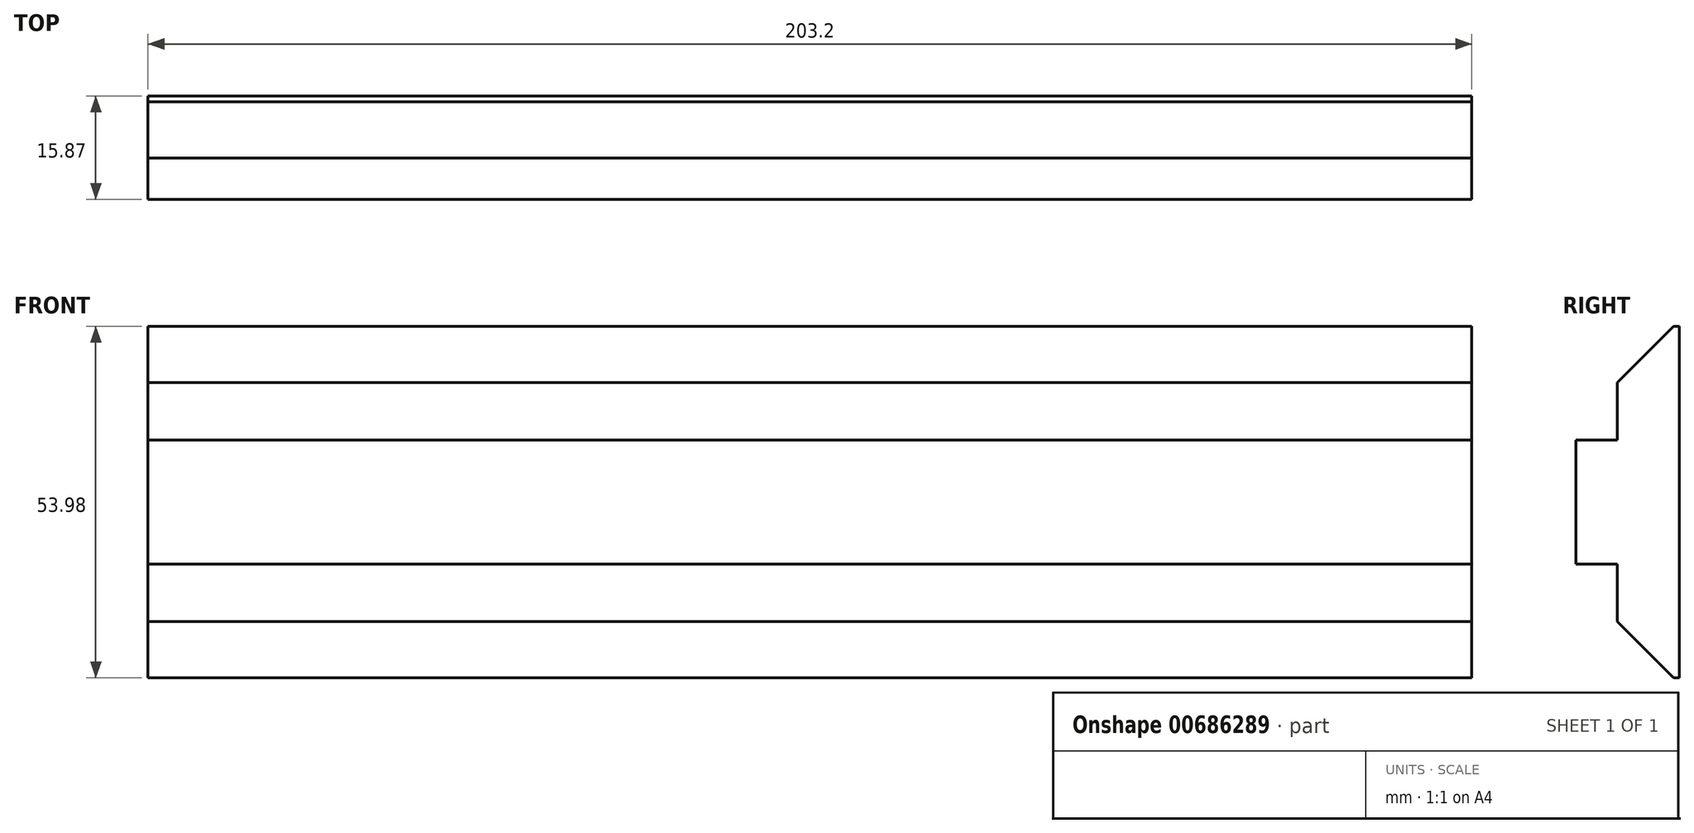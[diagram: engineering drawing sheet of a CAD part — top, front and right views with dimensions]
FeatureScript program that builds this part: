
annotation { "Feature Type Name" : "Feature", "Feature Type Description" : "" }
export const myFeature = defineFeature(function(context is Context, id is Id, definition is map)
    precondition{}
    {
        {
            var Q0;
            Q0=qCreatedBy(makeId("Front.planeOp"),FACE);
            var sketch = newSketch(context, id + "F0", { "sketchPlane" : qUnion([Q0])});
            skLineSegment(sketch, "E0.bottom", {"start": v(101.6, 26.99) * mm, "end": v(-101.6, 26.99) * mm});
            skLineSegment(sketch, "E0.top", {"start": v(101.6, -26.99) * mm, "end": v(-101.6, -26.99) * mm});
            skLineSegment(sketch, "E0.left", {"start": v(101.6, 26.99) * mm, "end": v(101.6, -26.99) * mm});
            skLineSegment(sketch, "E0.right", {"start": v(-101.6, 26.99) * mm, "end": v(-101.6, -26.99) * mm});
            skPoint(sketch, "E0.middle", {"position": v(0, 0) * mm});
            skSolve(sketch);
        }
        {
            var Q0;
            Q0=makeQuery(id+"F0.imprint","IMPRINT",FACE,{"disambiguationData":[TD([[makeQuery(id+"F0.imprint","IMPRINT",EDGE,{"derivedFrom":sQuery(id+"F0.wireOp",EDGE,"E0.bottom")}),1.0]])]});
            extrude(context, id + "F1", {"entities" : qUnion([Q0]), "endBound" : BoundingType.SYMMETRIC, "depth" : 9.52 * mm, "offsetDistance" : 25.4 * mm});
        }
        {
            var Q0;
            Q0=makeQuery(id+"F1.opExtrude","CAP_EDGE",EDGE,{"disambiguationData":[OSD([sQuery(id+"F0.wireOp",EDGE,"E0.bottom")])],"isStart":false});
            var Q1;
            Q1=makeQuery(id+"F1.opExtrude","CAP_EDGE",EDGE,{"disambiguationData":[OSD([sQuery(id+"F0.wireOp",EDGE,"E0.top")])],"isStart":false});
            chamfer(context, id + "F2", {"entities" : qUnion([Q0, Q1]), "width" : 8.64 * mm, "tangentPropagation" : true});
        }
        {
            var Q0;
            Q0=makeQuery(id+"F1.opExtrude","CAP_FACE",FACE,{"disambiguationData":[OSD([sQuery(id+"F0.wireOp",EDGE,"E0.bottom"),sQuery(id+"F0.wireOp",EDGE,"E0.top"),sQuery(id+"F0.wireOp",EDGE,"E0.left"),sQuery(id+"F0.wireOp",EDGE,"E0.right")])],"isStart":false});
            var sketch = newSketch(context, id + "F3", { "sketchPlane" : qUnion([Q0])});
            skLineSegment(sketch, "E1.bottom", {"start": v(101.6, -9.52) * mm, "end": v(-101.6, -9.52) * mm});
            skLineSegment(sketch, "E1.top", {"start": v(101.6, 9.53) * mm, "end": v(-101.6, 9.53) * mm});
            skLineSegment(sketch, "E1.left", {"start": v(101.6, -9.52) * mm, "end": v(101.6, 9.53) * mm});
            skLineSegment(sketch, "E1.right", {"start": v(-101.6, -9.52) * mm, "end": v(-101.6, 9.53) * mm});
            skPoint(sketch, "E1.middle", {"position": v(0, 0) * mm});
            skSolve(sketch);
        }
        {
            var Q0;
            Q0=makeQuery(id+"F3.imprint","IMPRINT",FACE,{"disambiguationData":[TD([[makeQuery(id+"F3.imprint","IMPRINT",EDGE,{"derivedFrom":sQuery(id+"F3.wireOp",EDGE,"E1.bottom")}),-1.0]])]});
            extrude(context, id + "F4", {"entities" : qUnion([Q0]), "operationType" : NewBodyOperationType.ADD, "depth" : 6.35 * mm, "offsetDistance" : 25.4 * mm});
        }
    });
